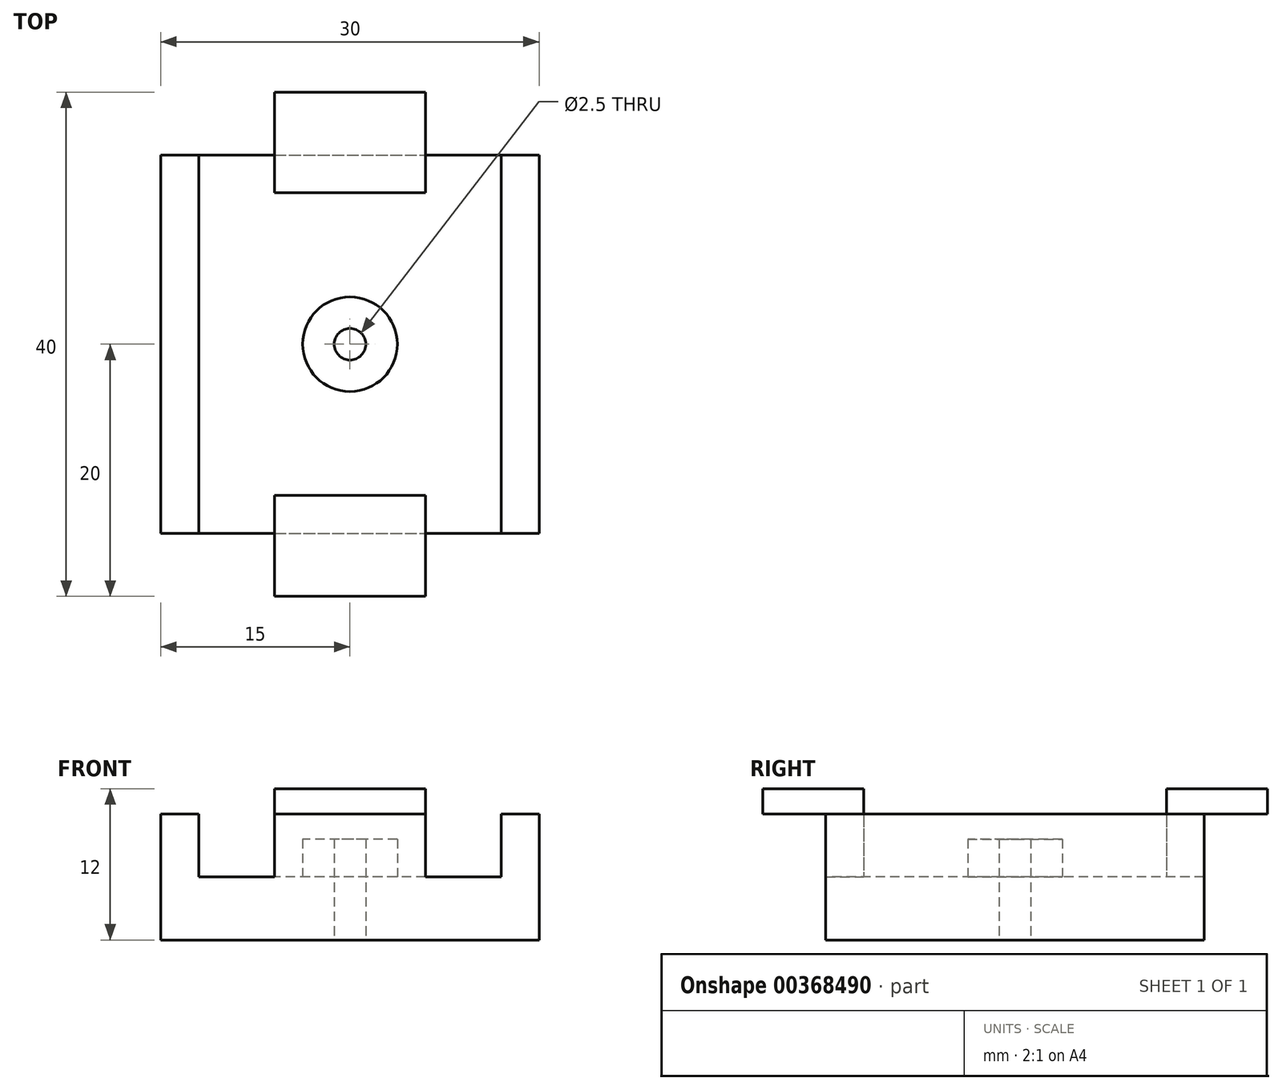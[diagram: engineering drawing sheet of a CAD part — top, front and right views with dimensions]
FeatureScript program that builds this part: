
annotation { "Feature Type Name" : "Feature", "Feature Type Description" : "" }
export const myFeature = defineFeature(function(context is Context, id is Id, definition is map)
    precondition{}
    {
        {
            var Q0;
            Q0=qCreatedBy(makeId("Top.planeOp"),FACE);
            var sketch = newSketch(context, id + "F0", { "sketchPlane" : qUnion([Q0])});
            skLineSegment(sketch, "E0.bottom", {"start": v(0, 0) * mm, "end": v(30, 0) * mm});
            skLineSegment(sketch, "E0.top", {"start": v(0, 30) * mm, "end": v(30, 30) * mm});
            skLineSegment(sketch, "E0.left", {"start": v(0, 0) * mm, "end": v(0, 30) * mm});
            skLineSegment(sketch, "E0.right", {"start": v(30, 0) * mm, "end": v(30, 30) * mm});
            skCircle(sketch, "E1", {"center": v(15, 15) * mm, "radius": 1.25 * mm});
            skSolve(sketch);
        }
        {
            var Q0;
            Q0 = qSketchRegion(id + "F0", true);
            extrude(context, id + "F1", {"entities" : qUnion([Q0]), "depth" : 5 * mm});
        }
        {
            var Q0;
            Q0=makeQuery(id+"F1.opExtrude","CAP_FACE",FACE,{"disambiguationData":[OSD([sQuery(id+"F0.wireOp",EDGE,"E0.bottom"),sQuery(id+"F0.wireOp",EDGE,"E0.top"),sQuery(id+"F0.wireOp",EDGE,"E0.left"),sQuery(id+"F0.wireOp",EDGE,"E0.right"),sQuery(id+"F0.wireOp",EDGE,"E1")])],"isStart":false});
            var sketch = newSketch(context, id + "F2", { "sketchPlane" : qUnion([Q0])});
            skLineSegment(sketch, "E2.bottom", {"start": v(0, 30) * mm, "end": v(3, 30) * mm});
            skLineSegment(sketch, "E2.top", {"start": v(0, 0) * mm, "end": v(3, 0) * mm});
            skLineSegment(sketch, "E2.left", {"start": v(0, 30) * mm, "end": v(0, 0) * mm});
            skLineSegment(sketch, "E2.right", {"start": v(3, 30) * mm, "end": v(3, 0) * mm});
            skLineSegment(sketch, "E3.bottom", {"start": v(30, 30) * mm, "end": v(27, 30) * mm});
            skLineSegment(sketch, "E3.top", {"start": v(30, 0) * mm, "end": v(27, 0) * mm});
            skLineSegment(sketch, "E3.left", {"start": v(30, 30) * mm, "end": v(30, 0) * mm});
            skLineSegment(sketch, "E3.right", {"start": v(27, 30) * mm, "end": v(27, 0) * mm});
            skLineSegment(sketch, "E4.bottom", {"start": v(15, 0) * mm, "end": v(21, 0) * mm});
            skLineSegment(sketch, "E4.top", {"start": v(15, 3) * mm, "end": v(21, 3) * mm});
            skLineSegment(sketch, "E4.right", {"start": v(21, 0) * mm, "end": v(21, 3) * mm});
            skLineSegment(sketch, "E5.MirrorCS", {"start": v(9, 30) * mm, "end": v(9, 27) * mm});
            skLineSegment(sketch, "E6.MirrorCS", {"start": v(15, 27) * mm, "end": v(9, 27) * mm});
            skLineSegment(sketch, "E7.MirrorCS", {"start": v(15, 30) * mm, "end": v(9, 30) * mm});
            skLineSegment(sketch, "E8.MirrorCS", {"start": v(15, 3) * mm, "end": v(9, 3) * mm});
            skLineSegment(sketch, "E9.MirrorCS", {"start": v(9, 0) * mm, "end": v(9, 3) * mm});
            skLineSegment(sketch, "E10.MirrorCS", {"start": v(15, 0) * mm, "end": v(9, 0) * mm});
            skCircle(sketch, "E11", {"center": v(15, 15) * mm, "radius": 3.75 * mm});
            skPoint(sketch, "E12", {"position": v(0, 0) * mm});
            skPoint(sketch, "E13", {"position": v(18, 30) * mm});
            skLineSegment(sketch, "E14.MirrorCS", {"start": v(15, 27) * mm, "end": v(21, 27) * mm});
            skLineSegment(sketch, "E15.MirrorCS", {"start": v(21, 30) * mm, "end": v(21, 27) * mm});
            skLineSegment(sketch, "E16.MirrorCS", {"start": v(15, 30) * mm, "end": v(21, 30) * mm});
            skSolve(sketch);
        }
        {
            var Q0;
            Q0=makeQuery(id+"F2.imprint","IMPRINT",FACE,{"disambiguationData":[TD([[makeQuery(id+"F2.imprint","IMPRINT",EDGE,{"derivedFrom":sQuery(id+"F2.wireOp",EDGE,"8fmn3nos-sJiJ-hjC9-k9d6-zAZhRcBgeBHC.bottom")}),-1.0]])]});
            var Q1;
            Q1=makeQuery(id+"F2.imprint","IMPRINT",FACE,{"disambiguationData":[TD([[makeQuery(id+"F2.imprint","IMPRINT",EDGE,{"derivedFrom":sQuery(id+"F2.wireOp",EDGE,"E2.bottom")}),-1.0]])]});
            var Q2;
            Q2=makeQuery(id+"F2.imprint","IMPRINT",FACE,{"disambiguationData":[TD([[makeQuery(id+"F2.imprint","IMPRINT",EDGE,{"derivedFrom":sQuery(id+"F2.wireOp",EDGE,"E3.bottom")}),-1.0]])]});
            var Q3;
            Q3=makeQuery(id+"F2.imprint","IMPRINT",FACE,{"disambiguationData":[TD([[makeQuery(id+"F2.imprint","IMPRINT",EDGE,{"derivedFrom":sQuery(id+"F2.wireOp",EDGE,"E4.bottom")}),1.0]])]});
            var Q4;
            Q4=makeQuery(id+"F2.imprint","IMPRINT",FACE,{"disambiguationData":[TD([[makeQuery(id+"F2.imprint","IMPRINT",EDGE,{"derivedFrom":sQuery(id+"F2.wireOp",EDGE,"E5.MirrorCS")}),1.0]])]});
            extrude(context, id + "F3", {"entities" : qUnion([Q0, Q1, Q2, Q3, Q4]), "operationType" : NewBodyOperationType.ADD, "depth" : 5 * mm});
        }
        {
            var Q0;
            Q0=makeQuery(id+"F2.imprint","IMPRINT",FACE,{"disambiguationData":[TD([[makeQuery(id+"F2.imprint","IMPRINT",EDGE,{"derivedFrom":sQuery(id+"F2.wireOp",EDGE,"E11")}),1.0]])]});
            var Q1;
            Q1=sQuery(id+"F2.wireOp",EDGE,"E11");
            extrude(context, id + "F4", {"entities" : qUnion([Q0]), "operationType" : NewBodyOperationType.ADD, "surfaceEntities" : qUnion([Q1]), "depth" : 3 * mm});
        }
        {
            var Q0;
            Q0=makeQuery(id+"F3.opExtrude","CAP_FACE",FACE,{"disambiguationData":[OSD([sQuery(id+"F2.wireOp",EDGE,"E4.bottom"),sQuery(id+"F2.wireOp",EDGE,"E4.top"),sQuery(id+"F2.wireOp",EDGE,"E4.right"),sQuery(id+"F2.wireOp",EDGE,"E8.MirrorCS"),sQuery(id+"F2.wireOp",EDGE,"E9.MirrorCS"),sQuery(id+"F2.wireOp",EDGE,"E10.MirrorCS")])],"isStart":false});
            var sketch = newSketch(context, id + "F5", { "sketchPlane" : qUnion([Q0])});
            skLineSegment(sketch, "E17.bottom", {"start": v(9, 3) * mm, "end": v(21, 3) * mm});
            skLineSegment(sketch, "E17.top", {"start": v(9, -5) * mm, "end": v(21, -5) * mm});
            skLineSegment(sketch, "E17.left", {"start": v(9, 3) * mm, "end": v(9, -5) * mm});
            skLineSegment(sketch, "E17.right", {"start": v(21, 3) * mm, "end": v(21, -5) * mm});
            skSolve(sketch);
        }
        {
            var Q0;
            {var subQ0=sQuery(id+"F5.wireOp",EDGE,"E17.bottom");Q0=makeQuery(id+"F5.imprint","IMPRINT",FACE,{"disambiguationData":[TD([[makeQuery(id+"F5.imprint","IMPRINT",EDGE,{"derivedFrom":subQ0}),-1.0]])]});}
            var Q1;
            {var subQ0=sQuery(id+"F5.wireOp",EDGE,"E17.top");Q1=makeQuery(id+"F5.imprint","IMPRINT",FACE,{"disambiguationData":[TD([[makeQuery(id+"F5.imprint","IMPRINT",EDGE,{"derivedFrom":subQ0}),1.0]])]});}
            extrude(context, id + "F6", {"entities" : qUnion([Q0, Q1]), "operationType" : NewBodyOperationType.ADD, "depth" : 2 * mm});
        }
        {
            var Q0;
            Q0=makeQuery(id+"F3.opExtrude","CAP_FACE",FACE,{"disambiguationData":[OSD([sQuery(id+"F2.wireOp",EDGE,"8fmn3nos-sJiJ-hjC9-k9d6-zAZhRcBgeBHC.bottom"),sQuery(id+"F2.wireOp",EDGE,"8fmn3nos-sJiJ-hjC9-k9d6-zAZhRcBgeBHC.top"),sQuery(id+"F2.wireOp",EDGE,"8fmn3nos-sJiJ-hjC9-k9d6-zAZhRcBgeBHC.right"),sQuery(id+"F2.wireOp",EDGE,"E5.MirrorCS"),sQuery(id+"F2.wireOp",EDGE,"E6.MirrorCS"),sQuery(id+"F2.wireOp",EDGE,"E7.MirrorCS")])],"isStart":false});
            var sketch = newSketch(context, id + "F7", { "sketchPlane" : qUnion([Q0])});
            skPoint(sketch, "E18.right.end.orphan", {"position": v(3, 35) * mm});
            skLineSegment(sketch, "E19.bottom", {"start": v(9, 27) * mm, "end": v(21, 27) * mm});
            skLineSegment(sketch, "E19.top", {"start": v(9, 35) * mm, "end": v(21, 35) * mm});
            skLineSegment(sketch, "E19.left", {"start": v(9, 27) * mm, "end": v(9, 35) * mm});
            skLineSegment(sketch, "E19.right", {"start": v(21, 27) * mm, "end": v(21, 35) * mm});
            skSolve(sketch);
        }
        {
            var Q0;
            {var subQ0=sQuery(id+"F7.wireOp",EDGE,"E19.top");Q0=makeQuery(id+"F7.imprint","IMPRINT",FACE,{"disambiguationData":[TD([[makeQuery(id+"F7.imprint","IMPRINT",EDGE,{"derivedFrom":subQ0}),-1.0]])]});}
            var Q1;
            {var subQ0=sQuery(id+"F7.wireOp",EDGE,"E19.bottom");Q1=makeQuery(id+"F7.imprint","IMPRINT",FACE,{"disambiguationData":[TD([[makeQuery(id+"F7.imprint","IMPRINT",EDGE,{"derivedFrom":subQ0}),-1.0]])]});}
            extrude(context, id + "F8", {"entities" : qUnion([Q0, Q1]), "operationType" : NewBodyOperationType.ADD, "depth" : 2 * mm});
        }
    });
